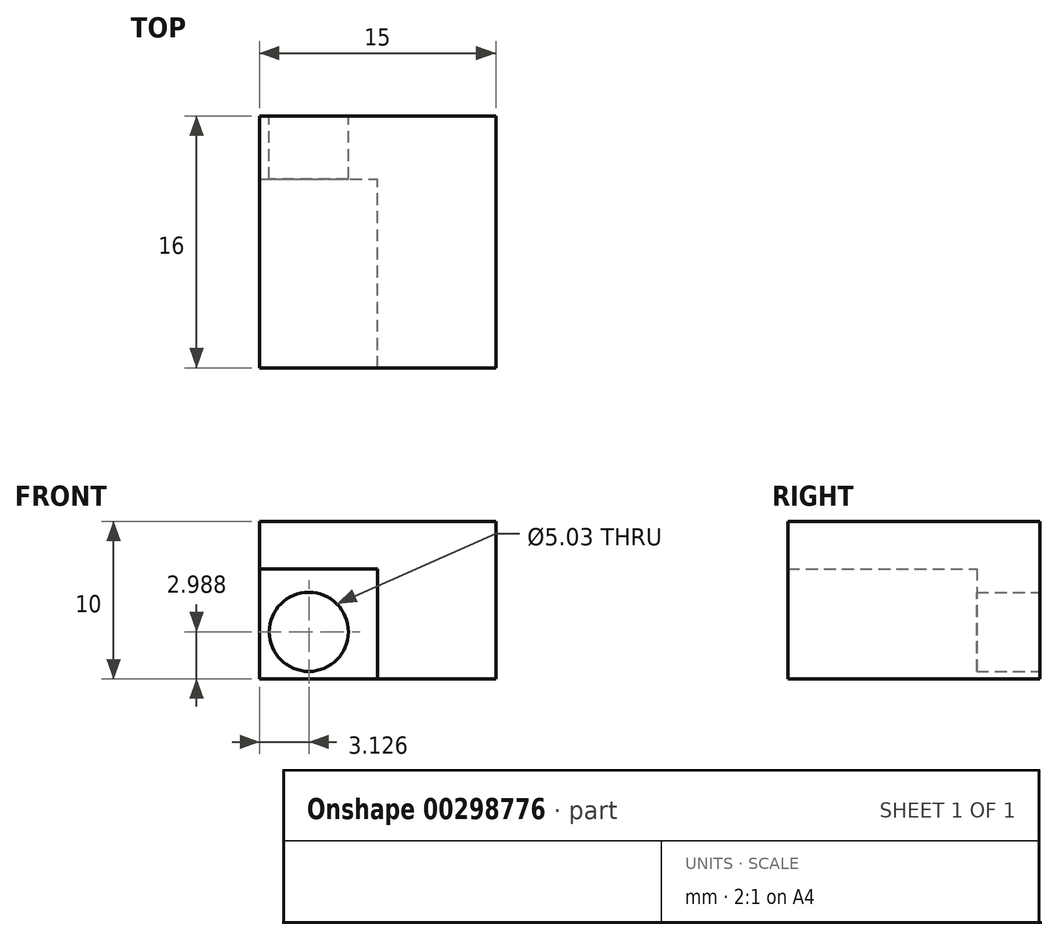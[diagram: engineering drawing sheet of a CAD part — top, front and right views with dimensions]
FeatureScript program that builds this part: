
annotation { "Feature Type Name" : "Feature", "Feature Type Description" : "" }
export const myFeature = defineFeature(function(context is Context, id is Id, definition is map)
    precondition{}
    {
        {
            var Q0;
            Q0=qCreatedBy(makeId("Front.planeOp"),FACE);
            var sketch = newSketch(context, id + "F0", { "sketchPlane" : qUnion([Q0])});
            skLineSegment(sketch, "E0", {"start": v(-51.66, 38.98) * mm, "end": v(-36.66, 38.98) * mm});
            skLineSegment(sketch, "E1", {"start": v(-36.66, 38.98) * mm, "end": v(-36.66, 28.98) * mm});
            skLineSegment(sketch, "E2", {"start": v(-36.66, 28.98) * mm, "end": v(-51.66, 28.98) * mm});
            skLineSegment(sketch, "E3", {"start": v(-51.66, 38.98) * mm, "end": v(-51.66, 28.98) * mm});
            skPoint(sketch, "E4", {"position": v(-51.66, 35.98) * mm});
            skLineSegment(sketch, "E5", {"start": v(-51.66, 35.98) * mm, "end": v(-44.16, 35.98) * mm});
            skPoint(sketch, "E6", {"position": v(-44.16, 28.98) * mm});
            skLineSegment(sketch, "E7", {"start": v(-44.16, 35.98) * mm, "end": v(-44.16, 28.98) * mm});
            skCircle(sketch, "E8", {"center": v(-48.53, 31.97) * mm, "radius": 2.51 * mm});
            skSolve(sketch);
        }
        {
            var Q0;
            {var subQ1=sQuery(id+"F0.wireOp",EDGE,"E0");Q0=makeQuery(id+"F0.imprint","IMPRINT",FACE,{"disambiguationData":[TD([[makeQuery(id+"F0.imprint","IMPRINT",EDGE,{"derivedFrom":subQ1}),-1.0]])]});}
            extrude(context, id + "F1", {"entities" : qUnion([Q0]), "depth" : 16 * mm});
        }
        {
            var Q0;
            {var subQ1=sQuery(id+"F0.wireOp",EDGE,"E5");Q0=makeQuery(id+"F0.imprint","IMPRINT",FACE,{"disambiguationData":[TD([[makeQuery(id+"F0.imprint","IMPRINT",EDGE,{"derivedFrom":subQ1}),-1.0]])]});}
            extrude(context, id + "F2", {"entities" : qUnion([Q0]), "operationType" : NewBodyOperationType.ADD, "depth" : 4 * mm});
        }
    });
